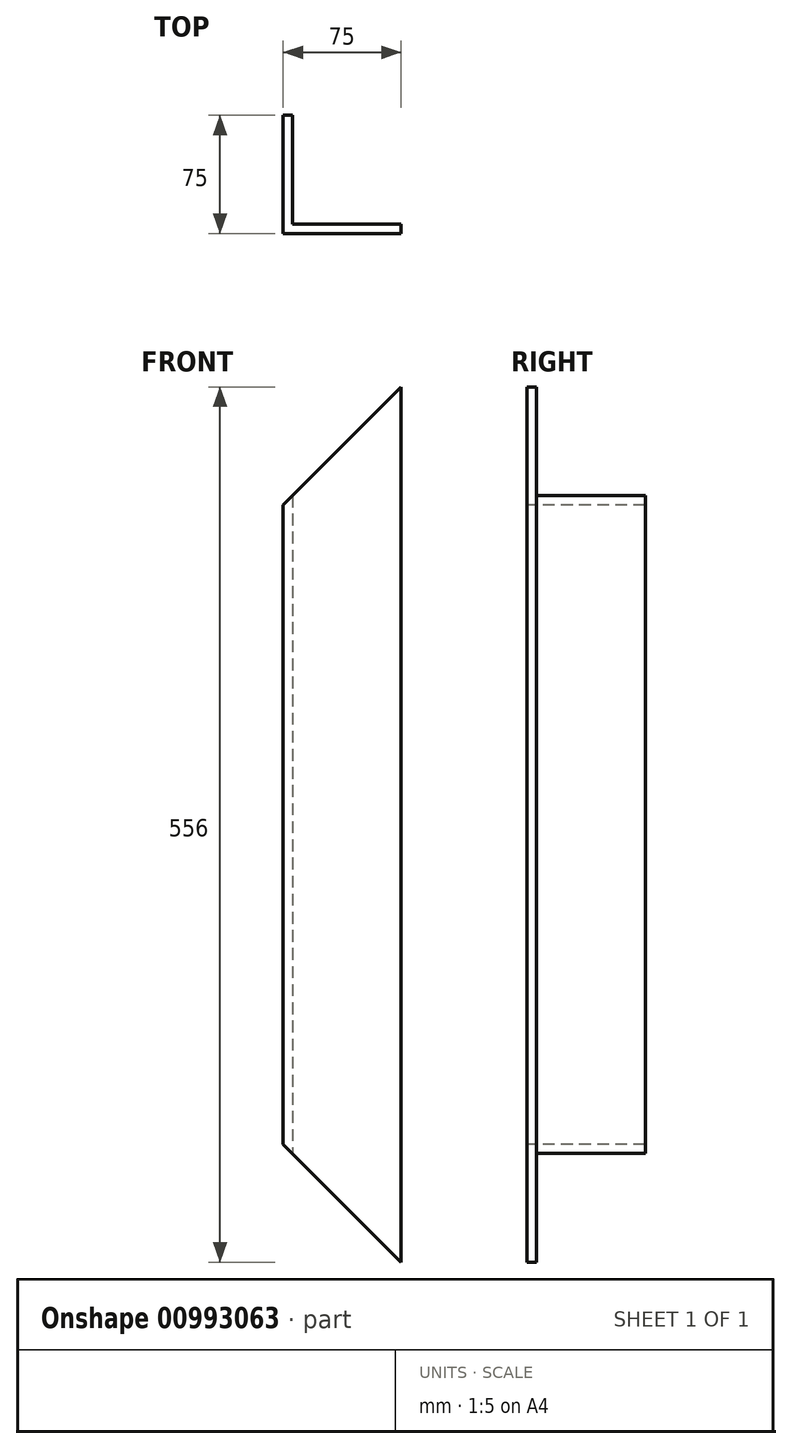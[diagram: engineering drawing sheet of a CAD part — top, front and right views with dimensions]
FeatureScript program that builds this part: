
annotation { "Feature Type Name" : "Feature", "Feature Type Description" : "" }
export const myFeature = defineFeature(function(context is Context, id is Id, definition is map)
    precondition{}
    {
        {
            var Q0;
            Q0=qCreatedBy(makeId("Top.planeOp"),FACE);
            var sketch = newSketch(context, id + "F0", { "sketchPlane" : qUnion([Q0])});
            skLineSegment(sketch, "E0", {"start": v(0, 0) * mm, "end": v(0, 75) * mm});
            skLineSegment(sketch, "E1", {"start": v(0, 75) * mm, "end": v(6, 75) * mm});
            skLineSegment(sketch, "E2", {"start": v(6, 75) * mm, "end": v(6, 6) * mm});
            skLineSegment(sketch, "E3", {"start": v(6, 6) * mm, "end": v(75, 6) * mm});
            skLineSegment(sketch, "E4", {"start": v(75, 6) * mm, "end": v(75, 0) * mm});
            skLineSegment(sketch, "E5", {"start": v(75, 0) * mm, "end": v(0, 0) * mm});
            skSolve(sketch);
        }
        {
            var Q0;
            Q0=makeQuery(id+"F0.imprint","IMPRINT",FACE,{"disambiguationData":[TD([[makeQuery(id+"F0.imprint","IMPRINT",EDGE,{"derivedFrom":sQuery(id+"F0.wireOp",EDGE,"E0")}),-1.0]])]});
            extrude(context, id + "F1", {"entities" : qUnion([Q0]), "depth" : 556 * mm, "offsetDistance" : 25 * mm});
        }
        {
            var Q0;
            Q0=qCreatedBy(makeId("Front.planeOp"),FACE);
            var sketch = newSketch(context, id + "F2", { "sketchPlane" : qUnion([Q0])});
            skLineSegment(sketch, "E6", {"start": v(0, 0) * mm, "end": v(75, 0) * mm});
            skLineSegment(sketch, "E7", {"start": v(75, 0) * mm, "end": v(0, 75) * mm});
            skLineSegment(sketch, "E8", {"start": v(0, 75) * mm, "end": v(0, 0) * mm});
            skSolve(sketch);
        }
        {
            var Q0;
            Q0=makeQuery(id+"F2.imprint","IMPRINT",FACE,{"disambiguationData":[TD([[makeQuery(id+"F2.imprint","IMPRINT",EDGE,{"derivedFrom":sQuery(id+"F2.wireOp",EDGE,"E6")}),1.0]])]});
            extrude(context, id + "F3", {"entities" : qUnion([Q0]), "operationType" : NewBodyOperationType.REMOVE, "endBound" : BoundingType.THROUGH_ALL, "oppositeDirection" : true, "depth" : 25 * mm, "offsetDistance" : 25 * mm});
        }
        {
            var Q0;
            Q0=qCreatedBy(makeId("Front.planeOp"),FACE);
            var sketch = newSketch(context, id + "F4", { "sketchPlane" : qUnion([Q0])});
            skLineSegment(sketch, "E9", {"start": v(75, 556) * mm, "end": v(0, 481) * mm});
            skLineSegment(sketch, "E10", {"start": v(0, 481) * mm, "end": v(0, 556) * mm});
            skLineSegment(sketch, "E11", {"start": v(0, 556) * mm, "end": v(75, 556) * mm});
            skSolve(sketch);
        }
        {
            var Q0;
            Q0=makeQuery(id+"F4.imprint","IMPRINT",FACE,{"disambiguationData":[TD([[makeQuery(id+"F4.imprint","IMPRINT",EDGE,{"derivedFrom":sQuery(id+"F4.wireOp",EDGE,"E9")}),-1.0]])]});
            extrude(context, id + "F5", {"entities" : qUnion([Q0]), "operationType" : NewBodyOperationType.REMOVE, "endBound" : BoundingType.THROUGH_ALL, "oppositeDirection" : true, "depth" : 25 * mm, "offsetDistance" : 25 * mm});
        }
    });
